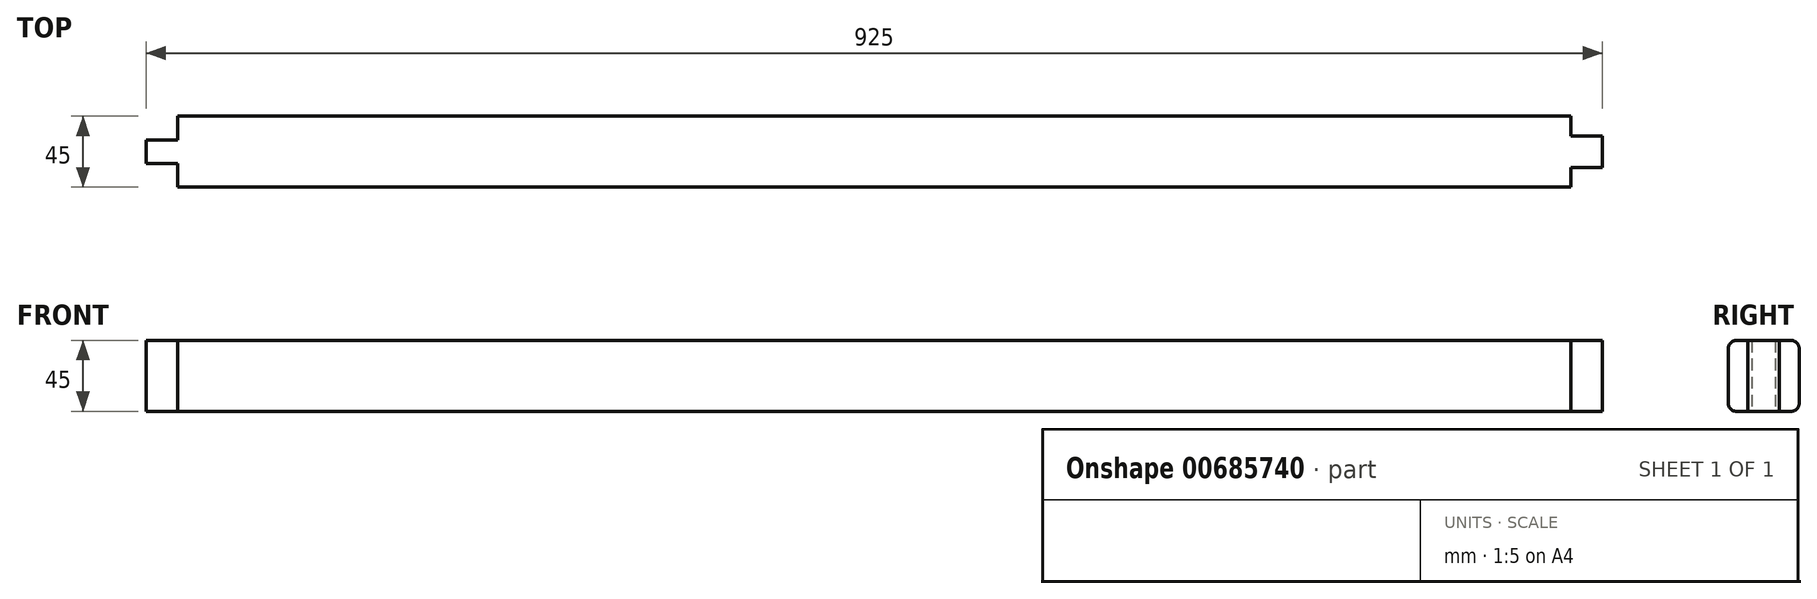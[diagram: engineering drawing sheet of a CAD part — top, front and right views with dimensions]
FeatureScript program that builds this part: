
annotation { "Feature Type Name" : "Feature", "Feature Type Description" : "" }
export const myFeature = defineFeature(function(context is Context, id is Id, definition is map)
    precondition{}
    {
        {
            var Q0;
            Q0=qCreatedBy(makeId("Right.planeOp"),FACE);
            var sketch = newSketch(context, id + "F0", { "sketchPlane" : qUnion([Q0])});
            skLineSegment(sketch, "E0.bottom", {"start": v(22.5, 22.5) * mm, "end": v(-22.5, 22.5) * mm});
            skLineSegment(sketch, "E0.top", {"start": v(22.5, -22.5) * mm, "end": v(-22.5, -22.5) * mm});
            skLineSegment(sketch, "E0.left", {"start": v(22.5, 22.5) * mm, "end": v(22.5, -22.5) * mm});
            skLineSegment(sketch, "E0.right", {"start": v(-22.5, 22.5) * mm, "end": v(-22.5, -22.5) * mm});
            skPoint(sketch, "E0.middle", {"position": v(0, 0) * mm});
            skSolve(sketch);
        }
        {
            var Q0;
            Q0=qSketchRegion(id+"F0",true);
            extrude(context, id + "F1", {"entities" : qUnion([Q0]), "endBound" : BoundingType.SYMMETRIC, "depth" : 885 * mm, "offsetDistance" : 25 * mm});
        }
        {
            var Q0;
            Q0=makeQuery(id+"F1.opExtrude","CAP_FACE",FACE,{"disambiguationData":[OSD([sQuery(id+"F0.wireOp",EDGE,"E0.bottom"),sQuery(id+"F0.wireOp",EDGE,"E0.top"),sQuery(id+"F0.wireOp",EDGE,"E0.left"),sQuery(id+"F0.wireOp",EDGE,"E0.right")])],"isStart":false});
            var sketch = newSketch(context, id + "F2", { "sketchPlane" : qUnion([Q0])});
            skLineSegment(sketch, "E1.bottom", {"start": v(10, 22.5) * mm, "end": v(-10, 22.5) * mm});
            skLineSegment(sketch, "E1.top", {"start": v(10, -22.5) * mm, "end": v(-10, -22.5) * mm});
            skLineSegment(sketch, "E1.left", {"start": v(10, 22.5) * mm, "end": v(10, -22.5) * mm});
            skLineSegment(sketch, "E1.right", {"start": v(-10, 22.5) * mm, "end": v(-10, -22.5) * mm});
            skPoint(sketch, "E1.middle", {"position": v(0, 0) * mm});
            skSolve(sketch);
        }
        {
            var Q0;
            Q0=qSketchRegion(id+"F2",true);
            extrude(context, id + "F3", {"entities" : qUnion([Q0]), "operationType" : NewBodyOperationType.ADD, "depth" : 20 * mm, "offsetDistance" : 25 * mm});
        }
        {
            var Q0;
            Q0=makeQuery(id+"F1.opExtrude","CAP_FACE",FACE,{"disambiguationData":[OSD([sQuery(id+"F0.wireOp",EDGE,"E0.bottom"),sQuery(id+"F0.wireOp",EDGE,"E0.top"),sQuery(id+"F0.wireOp",EDGE,"E0.left"),sQuery(id+"F0.wireOp",EDGE,"E0.right")])],"isStart":true});
            var sketch = newSketch(context, id + "F4", { "sketchPlane" : qUnion([Q0])});
            skLineSegment(sketch, "E2.bottom", {"start": v(7.5, 22.5) * mm, "end": v(-7.5, 22.5) * mm});
            skLineSegment(sketch, "E2.top", {"start": v(7.5, -22.5) * mm, "end": v(-7.5, -22.5) * mm});
            skLineSegment(sketch, "E2.left", {"start": v(7.5, 22.5) * mm, "end": v(7.5, -22.5) * mm});
            skLineSegment(sketch, "E2.right", {"start": v(-7.5, 22.5) * mm, "end": v(-7.5, -22.5) * mm});
            skPoint(sketch, "E2.middle", {"position": v(0, 0) * mm});
            skSolve(sketch);
        }
        {
            var Q0;
            Q0=qSketchRegion(id+"F4",true);
            extrude(context, id + "F5", {"entities" : qUnion([Q0]), "operationType" : NewBodyOperationType.ADD, "depth" : 20 * mm, "offsetDistance" : 25 * mm});
        }
        {
            var Q0;
            Q0=makeQuery(id+"F1.opExtrude","SWEPT_EDGE",EDGE,{"disambiguationData":[OSD([sQuery(id+"F0.wireOp",EDGE,"E0.bottom"),sQuery(id+"F0.wireOp",EDGE,"E0.right")])]});
            var Q1;
            Q1=makeQuery(id+"F1.opExtrude","SWEPT_EDGE",EDGE,{"disambiguationData":[OSD([sQuery(id+"F0.wireOp",EDGE,"E0.bottom"),sQuery(id+"F0.wireOp",EDGE,"E0.left")])]});
            var Q2;
            Q2=makeQuery(id+"F1.opExtrude","SWEPT_EDGE",EDGE,{"disambiguationData":[OSD([sQuery(id+"F0.wireOp",EDGE,"E0.top"),sQuery(id+"F0.wireOp",EDGE,"E0.right")])]});
            var Q3;
            Q3=makeQuery(id+"F1.opExtrude","SWEPT_EDGE",EDGE,{"disambiguationData":[OSD([sQuery(id+"F0.wireOp",EDGE,"E0.top"),sQuery(id+"F0.wireOp",EDGE,"E0.left")])]});
            fillet(context, id + "F6", {"entities" : qUnion([Q0, Q1, Q2, Q3]), "radius" : 5 * mm, "tangentPropagation" : true, "allowEdgeOverflow" : false});
        }
    });
